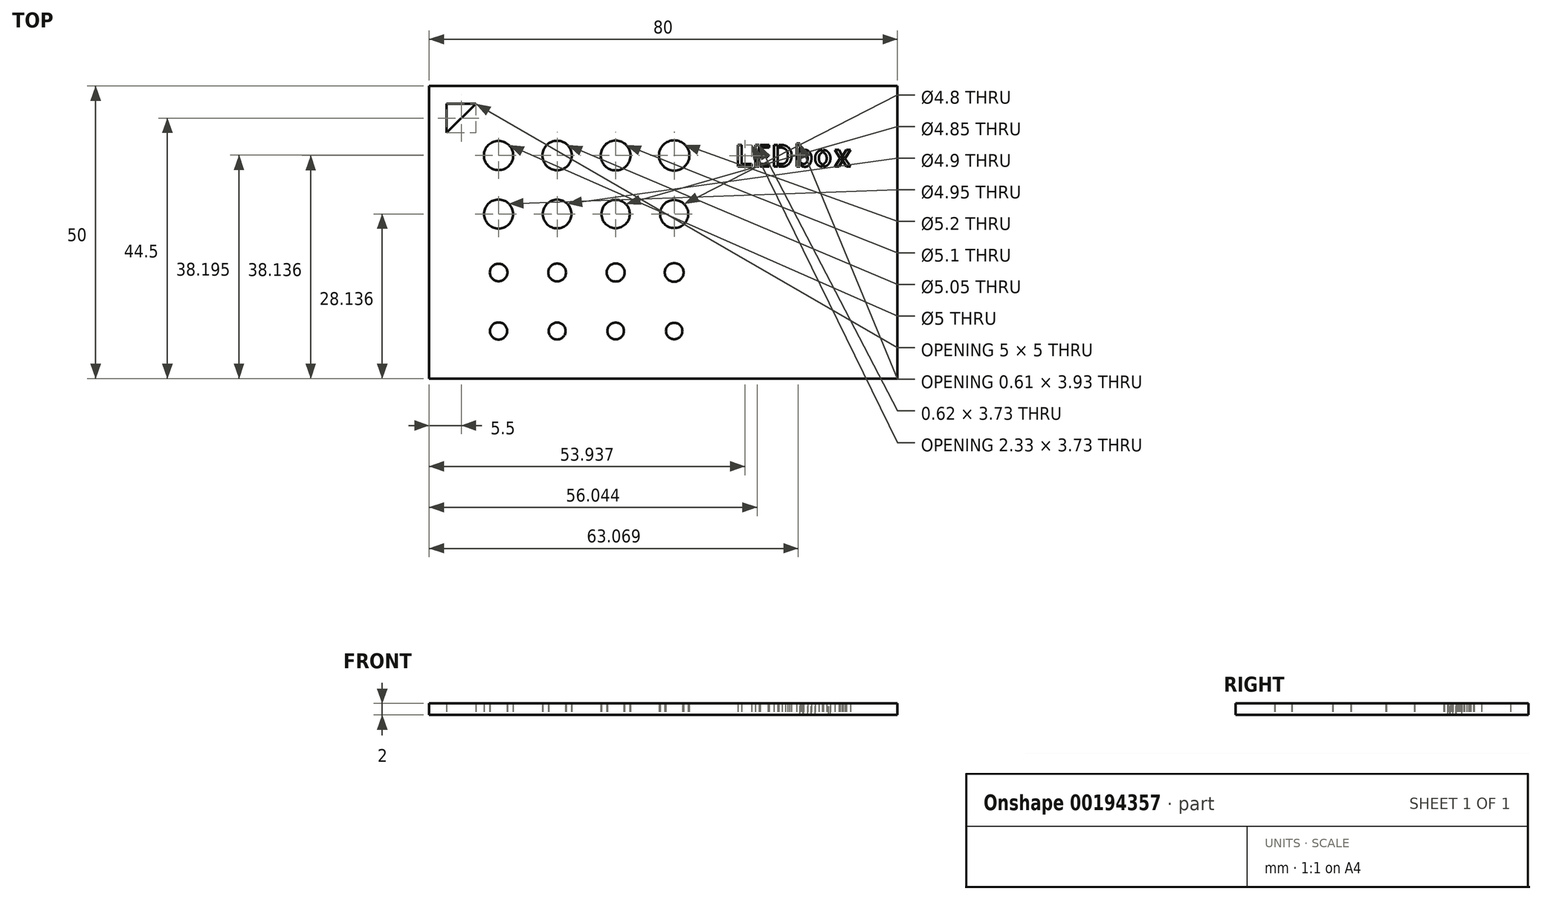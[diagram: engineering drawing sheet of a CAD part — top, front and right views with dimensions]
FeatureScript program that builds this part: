
annotation { "Feature Type Name" : "Feature", "Feature Type Description" : "" }
export const myFeature = defineFeature(function(context is Context, id is Id, definition is map)
    precondition{}
    {
        {
            var Q0;
            Q0=qCreatedBy(makeId("Top.planeOp"),FACE);
            var sketch = newSketch(context, id + "F0", { "sketchPlane" : qUnion([Q0])});
            skLineSegment(sketch, "E0.bottom", {"start": v(-40, -25) * mm, "end": v(40, -25) * mm});
            skLineSegment(sketch, "E0.top", {"start": v(-40, 25) * mm, "end": v(40, 25) * mm});
            skLineSegment(sketch, "E0.left", {"start": v(-40, -25) * mm, "end": v(-40, 25) * mm});
            skLineSegment(sketch, "E0.right", {"start": v(40, -25) * mm, "end": v(40, 25) * mm});
            skPoint(sketch, "E0.middle", {"position": v(0, 0) * mm});
            skCircle(sketch, "E1", {"center": v(-28.14, 13.14) * mm, "radius": 2.5 * mm});
            skLineSegment(sketch, "E2", {"start": v(-37, 22) * mm, "end": v(-37, 17) * mm});
            skLineSegment(sketch, "E3", {"start": v(-37, 17) * mm, "end": v(-32, 22) * mm});
            skLineSegment(sketch, "E4", {"start": v(-32, 22) * mm, "end": v(-37, 22) * mm});
            skCircle(sketch, "E5", {"center": v(-18.14, 13.14) * mm, "radius": 2.52 * mm});
            skCircle(sketch, "E6", {"center": v(-8.14, 13.14) * mm, "radius": 2.55 * mm});
            skCircle(sketch, "E7", {"center": v(1.86, 13.14) * mm, "radius": 2.6 * mm});
            skCircle(sketch, "E8", {"center": v(-28.14, 3.14) * mm, "radius": 2.48 * mm});
            skCircle(sketch, "E9", {"center": v(-18.14, 3.14) * mm, "radius": 2.45 * mm});
            skCircle(sketch, "E10", {"center": v(-8.14, 3.14) * mm, "radius": 2.43 * mm});
            skCircle(sketch, "E11", {"center": v(1.86, 3.14) * mm, "radius": 2.4 * mm});
            skCircle(sketch, "E12", {"center": v(-28.14, -6.86) * mm, "radius": 1.5 * mm});
            skCircle(sketch, "E13", {"center": v(-18.14, -6.86) * mm, "radius": 1.52 * mm});
            skCircle(sketch, "E14", {"center": v(-8.14, -6.86) * mm, "radius": 1.55 * mm});
            skCircle(sketch, "E15", {"center": v(1.86, -6.86) * mm, "radius": 1.6 * mm});
            skCircle(sketch, "E16", {"center": v(-28.14, -16.86) * mm, "radius": 1.48 * mm});
            skCircle(sketch, "E17", {"center": v(-18.14, -16.86) * mm, "radius": 1.45 * mm});
            skCircle(sketch, "E18", {"center": v(-8.14, -16.86) * mm, "radius": 1.43 * mm});
            skCircle(sketch, "E19", {"center": v(1.86, -16.86) * mm, "radius": 1.4 * mm});
            skLineSegment(sketch, "E20", {"start": v(-34.5, 19.5) * mm, "end": v(-28.14, 13.14) * mm});
            skText(sketch, "E21", { "text": "LEDbox", "fontName": "AllertaStencil-Regular.ttf"});
            const initialGuessF0  = {"E21": [0.0123, 0.01123, 1, 0, 0.00373]};
            skSetInitialGuess(sketch, initialGuessF0);
            skSolve(sketch);
        }
        {
            var Q0;
            Q0=makeQuery(id+"F0.imprint","IMPRINT",FACE,{"disambiguationData":[TD([[makeQuery(id+"F0.imprint","IMPRINT",EDGE,{"derivedFrom":sQuery(id+"F0.wireOp",EDGE,"E0.bottom")}),1.0]])]});
            extrude(context, id + "F1", {"entities" : qUnion([Q0]), "depth" : 2 * mm});
        }
    });
